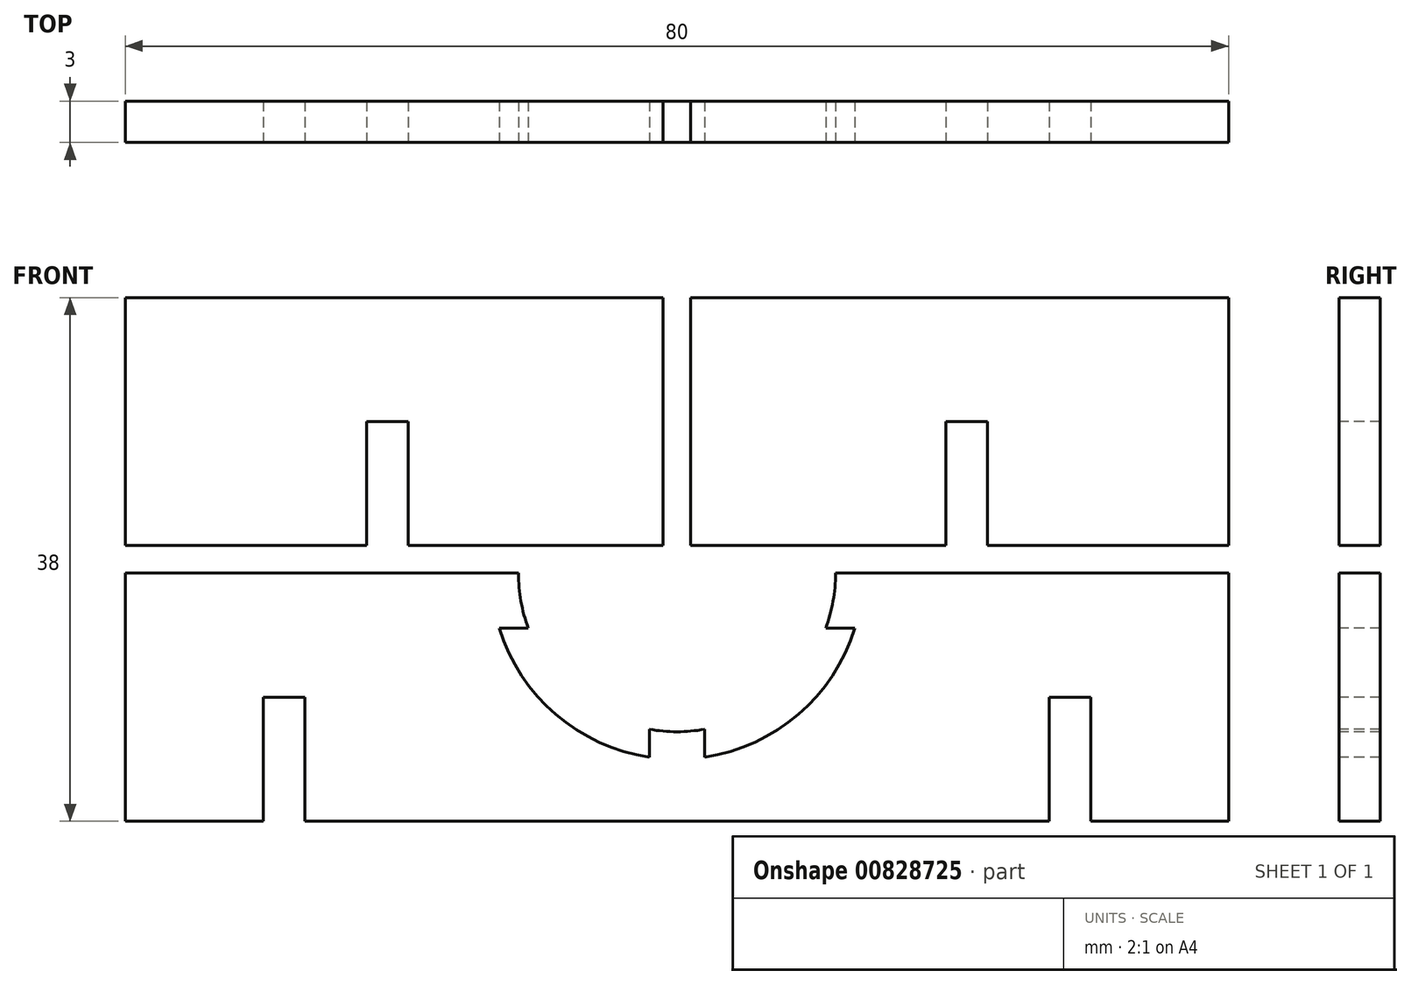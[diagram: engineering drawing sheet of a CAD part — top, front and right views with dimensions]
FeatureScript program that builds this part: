
annotation { "Feature Type Name" : "Feature", "Feature Type Description" : "" }
export const myFeature = defineFeature(function(context is Context, id is Id, definition is map)
    precondition{}
    {
        {
            var Q0;
            Q0=qCreatedBy(makeId("Front.planeOp"),FACE);
            var sketch = newSketch(context, id + "F0", { "sketchPlane" : qUnion([Q0])});
            skLineSegment(sketch, "E0.bottom", {"start": v(-40, -9) * mm, "end": v(40, -9) * mm});
            skLineSegment(sketch, "E0.top", {"start": v(-40, 9) * mm, "end": v(40, 9) * mm});
            skLineSegment(sketch, "E0.left", {"start": v(-40, -9) * mm, "end": v(-40, 9) * mm});
            skLineSegment(sketch, "E0.right", {"start": v(40, -9) * mm, "end": v(40, 9) * mm});
            skPoint(sketch, "E0.middle", {"position": v(0, 0) * mm});
            skSolve(sketch);
        }
        {
            var Q0;
            Q0 = qSketchRegion(id + "F0", true);
            extrude(context, id + "F1", {"entities" : qUnion([Q0]), "depth" : 3 * mm, "offsetDistance" : 25 * mm});
        }
        {
            var Q0;
            Q0=makeQuery(id+"F1.opExtrude","CAP_FACE",FACE,{"disambiguationData":[OSD([sQuery(id+"F0.wireOp",EDGE,"E0.bottom"),sQuery(id+"F0.wireOp",EDGE,"E0.top"),sQuery(id+"F0.wireOp",EDGE,"E0.left"),sQuery(id+"F0.wireOp",EDGE,"E0.right")])],"isStart":false});
            var sketch = newSketch(context, id + "F2", { "sketchPlane" : qUnion([Q0])});
            skCircle(sketch, "E1", {"center": v(0, 9) * mm, "radius": 11.5 * mm});
            skCircle(sketch, "E2", {"center": v(0, 9) * mm, "radius": 13.5 * mm});
            skLineSegment(sketch, "E3", {"start": v(-12.9, 5) * mm, "end": v(-10.78, 5) * mm});
            skLineSegment(sketch, "E4", {"start": v(-2, -2.32) * mm, "end": v(-2, -4.35) * mm});
            skLineSegment(sketch, "E5.MirrorCS", {"start": v(12.9, 5) * mm, "end": v(10.78, 5) * mm});
            skLineSegment(sketch, "E6.MirrorCS", {"start": v(2, -2.32) * mm, "end": v(2, -4.35) * mm});
            skLineSegment(sketch, "E7.bottom", {"start": v(-30, -9) * mm, "end": v(-27, -9) * mm});
            skLineSegment(sketch, "E7.top", {"start": v(-30, 0) * mm, "end": v(-27, 0) * mm});
            skLineSegment(sketch, "E7.left", {"start": v(-30, -9) * mm, "end": v(-30, 0) * mm});
            skLineSegment(sketch, "E7.right", {"start": v(-27, -9) * mm, "end": v(-27, 0) * mm});
            skLineSegment(sketch, "E8.MirrorCS", {"start": v(27, -9) * mm, "end": v(27, 0) * mm});
            skLineSegment(sketch, "E9.MirrorCS", {"start": v(30, -9) * mm, "end": v(30, 0) * mm});
            skLineSegment(sketch, "E10.MirrorCS", {"start": v(30, 0) * mm, "end": v(27, 0) * mm});
            skSolve(sketch);
        }
        {
            var Q0;
            {var subQ0=sQuery(id+"F2.wireOp",EDGE,"E3");Q0=makeQuery(id+"F2.imprint","IMPRINT",FACE,{"disambiguationData":[TD([[makeQuery(id+"F2.imprint","IMPRINT",EDGE,{"derivedFrom":subQ0}),-1.0]])]});}
            var Q1;
            {var subQ0=sQuery(id+"F2.wireOp",EDGE,"E5.MirrorCS");Q1=makeQuery(id+"F2.imprint","IMPRINT",FACE,{"disambiguationData":[TD([[makeQuery(id+"F2.imprint","IMPRINT",EDGE,{"derivedFrom":subQ0}),1.0]])]});}
            var Q2;
            Q2=makeQuery(id+"F2.imprint","IMPRINT",FACE,{"disambiguationData":[TD([[makeQuery(id+"F2.imprint","IMPRINT",EDGE,{"derivedFrom":sQuery(id+"F2.wireOp",EDGE,"E7.bottom")}),1.0]])]});
            var Q3;
            {var subQ0=sQuery(id+"F2.wireOp",EDGE,"E8.MirrorCS");Q3=makeQuery(id+"F2.imprint","IMPRINT",FACE,{"disambiguationData":[TD([[makeQuery(id+"F2.imprint","IMPRINT",EDGE,{"derivedFrom":subQ0}),-1.0]])]});}
            var Q4;
            {var subQ0=sQuery(id+"F2.wireOp",EDGE,"E1");var subQ4=makeQuery(id+"F2.imprint","INTERSECT",VERTEX,{"derivedFrom":[subQ0,sQuery(id+"F2.wireOp",EDGE,"E3")]});Q4=makeQuery(id+"F2.imprint","IMPRINT",FACE,{"disambiguationData":[TD([[makeQuery(id+"F2.imprint","IMPRINT",EDGE,{"disambiguationData":[TD([[subQ4,1.0]])],"derivedFrom":subQ0}),1.0]])]});}
            extrude(context, id + "F3", {"entities" : qUnion([Q0, Q1, Q2, Q3, Q4]), "operationType" : NewBodyOperationType.REMOVE, "endBound" : BoundingType.UP_TO_NEXT, "oppositeDirection" : true, "depth" : 25 * mm, "offsetDistance" : 25 * mm});
        }
        {
            var Q0;
            Q0=qCreatedBy(makeId("Front.planeOp"),FACE);
            var sketch = newSketch(context, id + "F4", { "sketchPlane" : qUnion([Q0])});
            skLineSegment(sketch, "E11.bottom", {"start": v(-40, 29) * mm, "end": v(-1, 29) * mm});
            skLineSegment(sketch, "E11.top", {"start": v(-40, 11) * mm, "end": v(-1, 11) * mm});
            skLineSegment(sketch, "E11.left", {"start": v(-40, 29) * mm, "end": v(-40, 11) * mm});
            skLineSegment(sketch, "E11.right", {"start": v(-1, 29) * mm, "end": v(-1, 11) * mm});
            skLineSegment(sketch, "E12.MirrorCS", {"start": v(40, 29) * mm, "end": v(1, 29) * mm});
            skLineSegment(sketch, "E13.MirrorCS", {"start": v(1, 29) * mm, "end": v(1, 11) * mm});
            skLineSegment(sketch, "E14.MirrorCS", {"start": v(40, 11) * mm, "end": v(1, 11) * mm});
            skLineSegment(sketch, "E15.MirrorCS", {"start": v(40, 29) * mm, "end": v(40, 11) * mm});
            skSolve(sketch);
        }
        {
            var Q0;
            Q0 = qSketchRegion(id + "F4", true);
            extrude(context, id + "F5", {"entities" : qUnion([Q0]), "depth" : 3 * mm, "offsetDistance" : 25 * mm});
        }
        {
            var Q0;
            Q0=makeQuery(id+"F5.opExtrude","CAP_FACE",FACE,{"disambiguationData":[OSD([sQuery(id+"F4.wireOp",EDGE,"E11.bottom"),sQuery(id+"F4.wireOp",EDGE,"E11.top"),sQuery(id+"F4.wireOp",EDGE,"E11.left"),sQuery(id+"F4.wireOp",EDGE,"E11.right")])],"isStart":false});
            var sketch = newSketch(context, id + "F6", { "sketchPlane" : qUnion([Q0])});
            skLineSegment(sketch, "E16.bottom", {"start": v(-22.5, 11) * mm, "end": v(-19.5, 11) * mm});
            skLineSegment(sketch, "E16.top", {"start": v(-22.5, 20) * mm, "end": v(-19.5, 20) * mm});
            skLineSegment(sketch, "E16.left", {"start": v(-22.5, 11) * mm, "end": v(-22.5, 20) * mm});
            skLineSegment(sketch, "E16.right", {"start": v(-19.5, 11) * mm, "end": v(-19.5, 20) * mm});
            skLineSegment(sketch, "E17.MirrorCS", {"start": v(22.5, 11) * mm, "end": v(22.5, 20) * mm});
            skLineSegment(sketch, "E18.MirrorCS", {"start": v(22.5, 20) * mm, "end": v(19.5, 20) * mm});
            skLineSegment(sketch, "E19.MirrorCS", {"start": v(19.5, 11) * mm, "end": v(19.5, 20) * mm});
            skSolve(sketch);
        }
        {
            var Q0;
            Q0=makeQuery(id+"F6.imprint","IMPRINT",FACE,{"disambiguationData":[TD([[makeQuery(id+"F6.imprint","IMPRINT",EDGE,{"derivedFrom":sQuery(id+"F6.wireOp",EDGE,"E16.bottom")}),1.0]])]});
            extrude(context, id + "F7", {"entities" : qUnion([Q0]), "operationType" : NewBodyOperationType.REMOVE, "endBound" : BoundingType.UP_TO_NEXT, "oppositeDirection" : true, "depth" : 25 * mm, "offsetDistance" : 25 * mm});
        }
        {
            var Q0;
            Q0=makeQuery(id+"F5.opExtrude","CAP_FACE",FACE,{"disambiguationData":[OSD([sQuery(id+"F4.wireOp",EDGE,"E12.MirrorCS"),sQuery(id+"F4.wireOp",EDGE,"E13.MirrorCS"),sQuery(id+"F4.wireOp",EDGE,"E14.MirrorCS"),sQuery(id+"F4.wireOp",EDGE,"E15.MirrorCS")])],"isStart":false});
            var sketch = newSketch(context, id + "F8", { "sketchPlane" : qUnion([Q0])});
            skLineSegment(sketch, "E20.bottom", {"start": v(19.5, 20) * mm, "end": v(22.5, 20) * mm});
            skLineSegment(sketch, "E20.top", {"start": v(19.5, 11) * mm, "end": v(22.5, 11) * mm});
            skLineSegment(sketch, "E20.left", {"start": v(19.5, 20) * mm, "end": v(19.5, 11) * mm});
            skLineSegment(sketch, "E20.right", {"start": v(22.5, 20) * mm, "end": v(22.5, 11) * mm});
            skSolve(sketch);
        }
        {
            var Q0;
            Q0 = qSketchRegion(id + "F8", true);
            extrude(context, id + "F9", {"entities" : qUnion([Q0]), "operationType" : NewBodyOperationType.REMOVE, "endBound" : BoundingType.UP_TO_NEXT, "oppositeDirection" : true, "depth" : 25 * mm, "offsetDistance" : 25 * mm});
        }
    });
